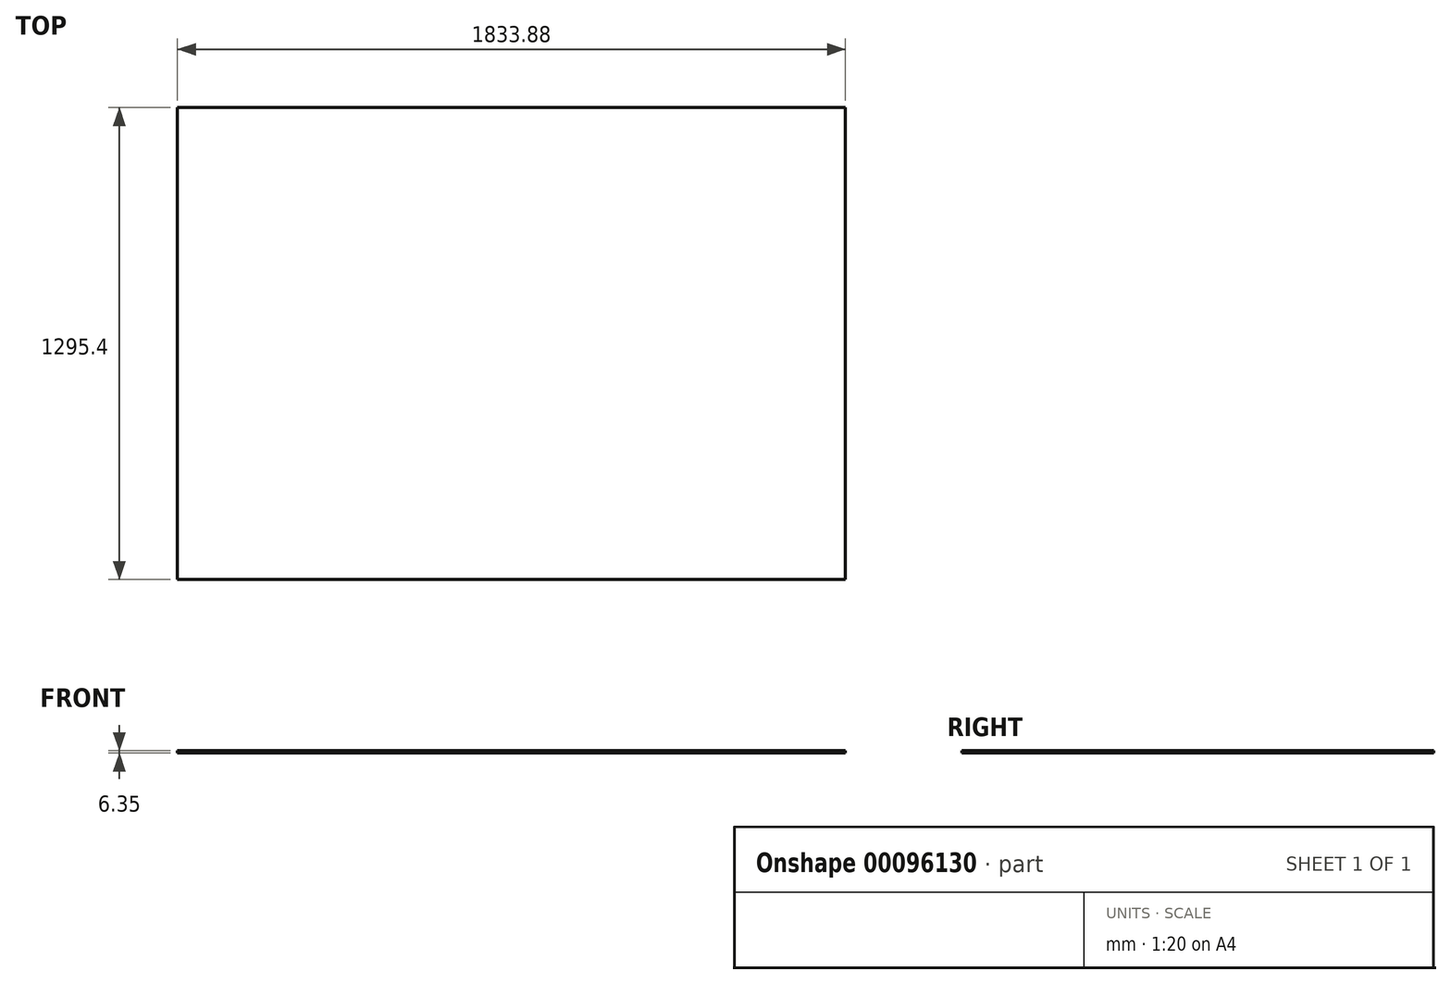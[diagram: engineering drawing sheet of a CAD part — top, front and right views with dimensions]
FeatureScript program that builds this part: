
annotation { "Feature Type Name" : "Feature", "Feature Type Description" : "" }
export const myFeature = defineFeature(function(context is Context, id is Id, definition is map)
    precondition{}
    {
        {
            var Q0;
            Q0=qCreatedBy(makeId("Top.planeOp"),FACE);
            var sketch = newSketch(context, id + "F0", { "sketchPlane" : qUnion([Q0])});
            skLineSegment(sketch, "E0.bottom", {"start": v(0, 0) * mm, "end": v(1833.88, 0) * mm});
            skLineSegment(sketch, "E0.top", {"start": v(0, 1295.4) * mm, "end": v(1833.88, 1295.4) * mm});
            skLineSegment(sketch, "E0.left", {"start": v(0, 0) * mm, "end": v(0, 1295.4) * mm});
            skLineSegment(sketch, "E0.right", {"start": v(1833.88, 0) * mm, "end": v(1833.88, 1295.4) * mm});
            skSolve(sketch);
        }
        {
            var Q0;
            Q0=makeQuery(id+"F0.imprint","IMPRINT",FACE,{"disambiguationData":[TD([[makeQuery(id+"F0.imprint","IMPRINT",EDGE,{"derivedFrom":sQuery(id+"F0.wireOp",EDGE,"E0.bottom")}),1.0]])]});
            extrude(context, id + "F1", {"entities" : qUnion([Q0]), "depth" : 6.35 * mm});
        }
    });
